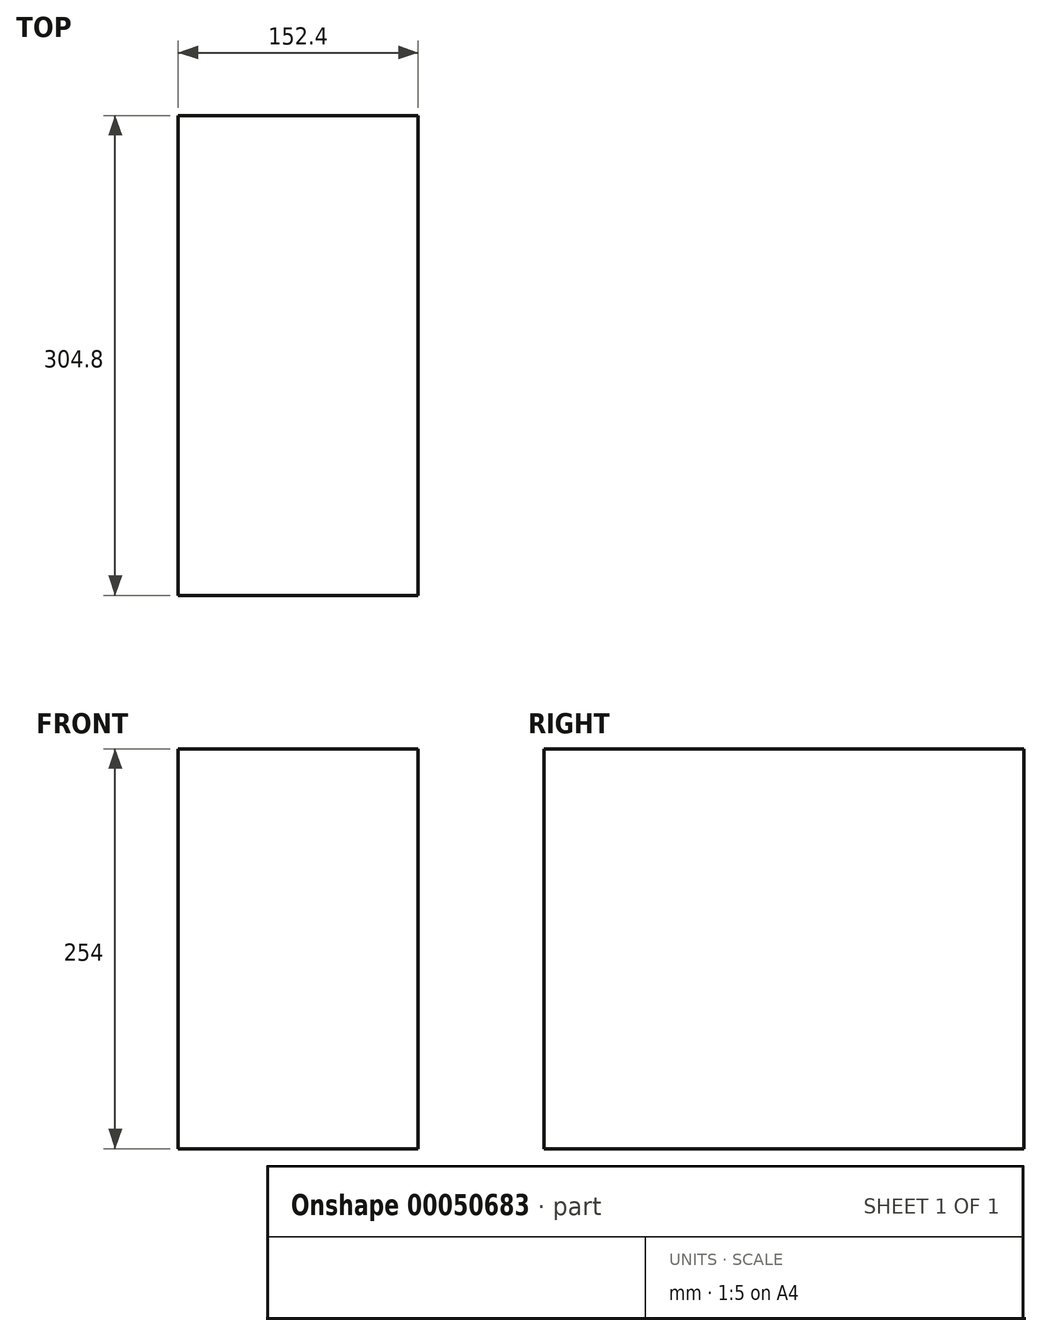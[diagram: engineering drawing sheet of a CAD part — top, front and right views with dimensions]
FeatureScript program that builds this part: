
annotation { "Feature Type Name" : "Feature", "Feature Type Description" : "" }
export const myFeature = defineFeature(function(context is Context, id is Id, definition is map)
    precondition{}
    {
        {
            var Q0;
            Q0=qCreatedBy(makeId("Front.planeOp"),FACE);
            var sketch = newSketch(context, id + "F0", { "sketchPlane" : qUnion([Q0])});
            skLineSegment(sketch, "E0.bottom", {"start": v(0, 0) * mm, "end": v(152.4, 0) * mm});
            skLineSegment(sketch, "E0.top", {"start": v(0, 254) * mm, "end": v(152.4, 254) * mm});
            skLineSegment(sketch, "E0.left", {"start": v(0, 0) * mm, "end": v(0, 254) * mm});
            skLineSegment(sketch, "E0.right", {"start": v(152.4, 0) * mm, "end": v(152.4, 254) * mm});
            skSolve(sketch);
        }
        {
            var Q0;
            Q0 = qSketchRegion(id + "F0", true);
            extrude(context, id + "F1", {"entities" : qUnion([Q0]), "depth" : 304.8 * mm});
        }
    });
